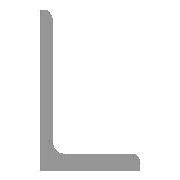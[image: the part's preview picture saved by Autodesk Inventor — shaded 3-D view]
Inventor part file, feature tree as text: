
AUTODESK INVENTOR PART (.ipt)
format: ipt  version: 2024.3 (Build 283343000, 343)  size: 465,408 bytes
history: native  units: mm (DEFAULTED — no unit token found)
features: sketch x9, hole x5, other x5, sheet_metal_op x4, chamfer x2, projected_geometry x1
ambient origin geometry x8: Origin, YZ Plane, XZ Plane, XY Plane, X Axis, Y Axis, Z Axis, Center Point
bodies: Body1 (feature_tree)
feature tree (26):
  sheet_metal_op  "Face1"
  sheet_metal_op  "Flange1"
  hole  "Hole6"  [1 undecoded]
  hole  "Hole7"  [1 undecoded]
  hole  "Hole8"  [1 undecoded]
  hole  "Hole9"  [1 undecoded]
  chamfer  "Corner Round1"
  chamfer  "Corner Round2"
  hole  "Hole10"  [1 undecoded]
  sketch  "Sketch13"  dims[d119=749.3mm d120=63.5mm]
  other  "Plate1"
  sketch  "Sketch14"  dims[d121=4.7625mm d122=4.7625mm]
  other  "Plate2"
  sheet_metal_op  "Bend1"
  sheet_metal_op  "Corner1"
  sketch  "Sketch15"  dims[d123=2.38125mm d124=9.525mm]
  projected_geometry  "Projected Loop3"
  sketch  "Sketch16"  dims[d125=7.14375mm d126=38.1mm d127=90.0deg d128=3.175mm]
  sketch  "Sketch17"  dims[d129=19.05mm d130=4.7625mm]
  sketch  "Sketch18"  dims[d131=7.14375mm]
  sketch  "Sketch19"  dims[d132=45.0deg]
  sketch  "Sketch20"  dims[d134=127.0mm]
  sketch  "Sketch21"  dims[d135=25.4mm d136=9.525mm d137=12.217305mm d138=6.35mm d139=546.1mm d140=12.7mm d141=8.726646mm d142=6.35mm d143=3.175mm d144=4.7625mm d145=0.0mm d146=64.9859mm d147=28.575mm d148=558.8mm d149=28.575mm d150=19.05mm d151=9.779mm d152=1.9558mm d153=14.3117mm d154=4.7625mm d155=20.594885mm d156=15.08125mm d157=8.73125mm d158=38.1mm d159=76.2mm d160=50.0mm d162=149.225mm d163=10.0mm d165=25.4mm d167=38.1mm d168=4.7625mm d169=0.0mm d170=25.4mm d171=16.248527mm d173=139.7mm d174=40.0mm d176=12.7mm d177=10.0mm d179=25.4mm d181=4.9784mm d182=19.05mm d183=9.779mm d184=6.35mm d185=14.3117mm d186=25.4mm d187=20.594885mm d188=12.7mm d189=14.2875mm d190=12.7mm d191=4.9784mm d192=19.05mm d193=9.525mm d194=6.35mm d195=14.3117mm d196=25.4mm d197=20.594885mm d198=20.0mm d200=723.9mm d201=10.0mm d203=25.4mm d205=12.7mm d206=139.7mm d207=3.9624mm d208=9.652mm d209=9.525mm d210=6.35mm d211=14.3117mm d212=25.4mm d213=20.594885mm d214=4.7625mm d215=6.35mm d216=15.5575mm d217=12.7mm d218=7.14375mm d219=3.9624mm d220=19.05mm d221=9.525mm d222=6.35mm d223=14.3117mm d224=4.7625mm d225=20.594885mm d226=15.5575mm d227=7.14375mm d228=12.7mm]
  other  "Cut1"
  other  "Cut2"
  other  "Definition1"
note: 5 required parameter values undecoded (feature->parameter linkage not recoverable at this tier; creation-order binding heuristic only, values carry confidence <= 0.55)
